AUTODESK INVENTOR PART (.ipt)
format: ipt  version: 2016 SP2 (Build 200236200, 236)  size: 5,327,872 bytes
history: native  units: mm
features: other x10, sketch x1
ambient origin geometry x8: Origin, YZ Plane, XZ Plane, XY Plane, X Axis, Y Axis, Z Axis, Center Point
bodies: Solid1 (feature_tree), Solid2 (feature_tree), Solid3 (feature_tree), Solid4 (feature_tree), Solid5 (feature_tree), Solid6 (feature_tree), Solid7 (feature_tree), Solid8 (feature_tree), Solid9 (feature_tree), Solid10 (feature_tree)
feature tree (11):
  sketch  "Sketch1"
  other  "CA_3_GS_telo-1-solid1"
  other  "CA_3_GS_pin-1-solid1"
  other  "CA_3_GS_pin-2-solid1"
  other  "CA_3_GS_pin-3-solid1"
  other  "CA_3_GS_pin-4-solid1"
  other  "CA_3_GS_screw-1-solid1"
  other  "CA_3_GS_screw-2-solid1"
  other  "CA_3_GS_screw-3-solid1"
  other  "CA_3_GS_screw-4-solid1"
  other  "CA_3_GS_tesnenie-1-solid1"
